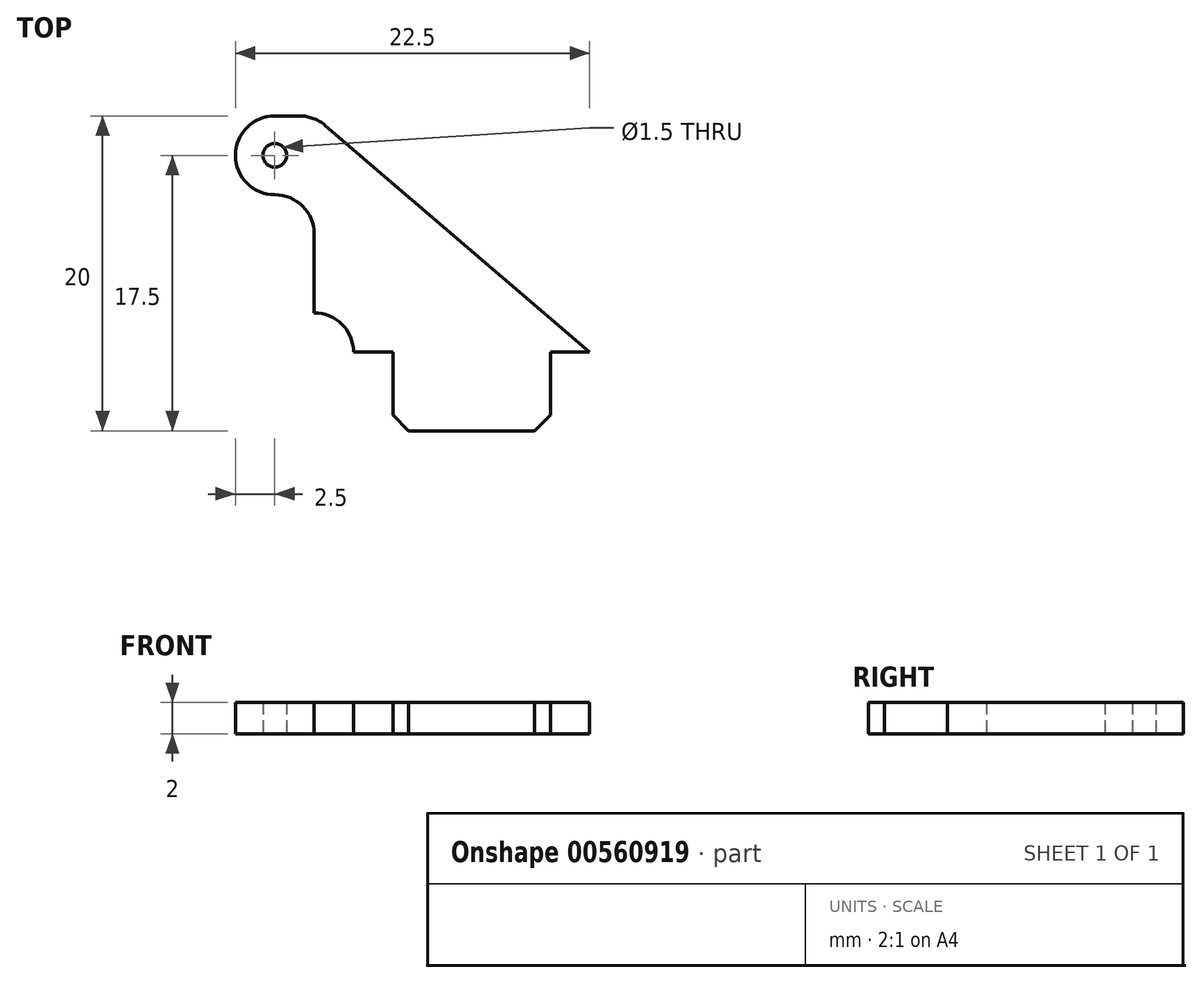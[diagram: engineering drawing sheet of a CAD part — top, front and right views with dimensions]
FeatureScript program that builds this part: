
annotation { "Feature Type Name" : "Feature", "Feature Type Description" : "" }
export const myFeature = defineFeature(function(context is Context, id is Id, definition is map)
    precondition{}
    {
        {
            var Q0;
            Q0=qCreatedBy(makeId("Top.planeOp"),FACE);
            var sketch = newSketch(context, id + "F0", { "sketchPlane" : qUnion([Q0])});
            skLineSegment(sketch, "E0.bottom", {"start": v(-7.5, -5) * mm, "end": v(2.5, -5) * mm});
            skLineSegment(sketch, "E0.top", {"start": v(-7.5, 0) * mm, "end": v(2.5, 0) * mm});
            skLineSegment(sketch, "E0.left", {"start": v(-7.5, -5) * mm, "end": v(-7.5, 0) * mm});
            skLineSegment(sketch, "E0.right", {"start": v(2.5, -5) * mm, "end": v(2.5, 0) * mm});
            skLineSegment(sketch, "E1", {"start": v(-7.5, 0) * mm, "end": v(-12.5, 0) * mm});
            skLineSegment(sketch, "E2", {"start": v(-12.5, 0) * mm, "end": v(-12.5, 10) * mm});
            skLineSegment(sketch, "E3", {"start": v(-12.5, 10) * mm, "end": v(-17.5, 10) * mm});
            skLineSegment(sketch, "E4", {"start": v(-17.5, 10) * mm, "end": v(-17.5, 15) * mm});
            skLineSegment(sketch, "E5", {"start": v(-17.5, 15) * mm, "end": v(-12.5, 15) * mm});
            skLineSegment(sketch, "E6", {"start": v(-12.5, 15) * mm, "end": v(5, 0) * mm});
            skLineSegment(sketch, "E7", {"start": v(5, 0) * mm, "end": v(2.5, 0) * mm});
            skCircle(sketch, "E8", {"center": v(-15, 12.5) * mm, "radius": 0.75 * mm});
            skCircle(sketch, "E9", {"center": v(-12.5, 0) * mm, "radius": 2.5 * mm});
            skLineSegment(sketch, "E10", {"start": v(-7.5, -4) * mm, "end": v(-6.5, -5) * mm});
            skLineSegment(sketch, "E11", {"start": v(2.5, -4) * mm, "end": v(1.5, -5) * mm});
            skSolve(sketch);
        }
        {
            var Q0;
            {var subQ5=sQuery(id+"F0.wireOp",EDGE,"E0.top");Q0=makeQuery(id+"F0.imprint","IMPRINT",FACE,{"disambiguationData":[TD([[makeQuery(id+"F0.imprint","IMPRINT",EDGE,{"derivedFrom":subQ5}),1.0]])]});}
            var Q1;
            {var subQ1=sQuery(id+"F0.wireOp",EDGE,"E0.top");Q1=makeQuery(id+"F0.imprint","IMPRINT",FACE,{"disambiguationData":[TD([[makeQuery(id+"F0.imprint","IMPRINT",EDGE,{"derivedFrom":subQ1}),-1.0]])]});}
            extrude(context, id + "F1", {"entities" : qUnion([Q0, Q1]), "depth" : 2 * mm, "offsetDistance" : 25 * mm});
        }
        {
            var Q0;
            Q0=makeQuery(id+"F1.opExtrude","SWEPT_EDGE",EDGE,{"disambiguationData":[OSD([sQuery(id+"F0.wireOp",EDGE,"E4"),sQuery(id+"F0.wireOp",EDGE,"E5")])]});
            var Q1;
            Q1=makeQuery(id+"F1.opExtrude","SWEPT_EDGE",EDGE,{"disambiguationData":[OSD([sQuery(id+"F0.wireOp",EDGE,"E3"),sQuery(id+"F0.wireOp",EDGE,"E4")])]});
            var Q2;
            Q2=makeQuery(id+"F1.opExtrude","SWEPT_EDGE",EDGE,{"disambiguationData":[OSD([sQuery(id+"F0.wireOp",EDGE,"E5"),sQuery(id+"F0.wireOp",EDGE,"E6")])]});
            var Q3;
            Q3=makeQuery(id+"F1.opExtrude","SWEPT_EDGE",EDGE,{"disambiguationData":[OSD([sQuery(id+"F0.wireOp",EDGE,"E2"),sQuery(id+"F0.wireOp",EDGE,"E3")])]});
            fillet(context, id + "F2", {"entities" : qUnion([Q0, Q1, Q2, Q3]), "radius" : 2.5 * mm, "tangentPropagation" : true, "allowEdgeOverflow" : false});
        }
    });
